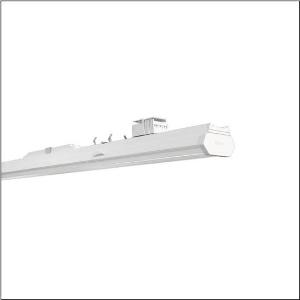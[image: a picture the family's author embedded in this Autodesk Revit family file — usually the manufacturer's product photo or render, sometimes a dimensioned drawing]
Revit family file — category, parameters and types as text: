
# Revit family: licross_r__21_protected_ho_52td13cn4c5s_0d58
name_source: partatom
category: Lighting Fixtures
units: mm (PartAtom-declared; Revit-internal decimal feet)

## family parameters
Cut with Voids When Loaded = No
Host = Face
Light Source = No
Part Type = Normal
Room Calculation Point = No
Round Connector Dimension = Use Diameter
Shared = No

## types (1)
- --- (1 x LED, 12680 lm, 68.9 W, 4000K)
    Apparent Load = 69 VA
    CIE Flux Codes = 89 96 99 100 99
    Color Rendering = 80
    Color Temperature = 4000K
    Default Elevation = 1800 mm
    Description = Licross® 21 Protected HO, luminaire insert, of sheet steel, galvanised, coil coated, white, length: 1.500mm, width: 66mm, height: 67mm, LED rated luminous flux: 12.690lm, light colour: 840, control gear: ON/OFF Multilumen, CLOi, control gear: ECG Multilumen, with plug, 3-pole, with phase selection, mains connection: 220..240V, AC, 50/60Hz, start of lifetime: 69W, end of service life: 83W, halogen-free wiring, primary light control with lens, of plastic, primary optical cover: cover, of PMMA, light emission: direct distribution, primary light characteristic: symmetric, protection rating (complete): IP54, insulation class (complete): insulation class I (protective earthing), certification: CE, ENEC, VDE, UKCA, protection symbol: D if used in an environment with non-conductive dust loads with corresponding accessories, impact resistance: IK06, permissible ambient temperature for indoor applications: -35..+35°C, corresponds to IFS (International Featured Standards) requirements for safety and quality in the food industry, reducing of maximum allowable ambient temperature of 5°C with ceiling mounting, LABS conformity tested according to VDMA 24364:2018-05, packaging unit: 1 piece
    Height = 92 mm
    Lamp = 1 x LED
    Lamp Light Flux = 12680 lm
    Lamp Power = 68.9 W
    Lamp count = 1
    Length = 1500 mm
    Luminous efficacy = 184 lm/W
    Manufacturer = Siteco
    ModVariant = No
    Model = 52TD13CN4C5S
    Mounting Place = Ceiling
    Mounting Type = Pendant
    Number of Poles = 1
    OnlyDefault = Yes
    Power Factor = 1
    Product Name = Licross® 21 Protected HO
    Product group = luminaire insert
    ProductGroupID = 901
    Protection Class = Protection class I
    Protection Degree = IP 54
    RLX_Detail_Level = 1
    RLX_Emergency_Light_Flux = 0 lm
    RLX_Emergency_Type = 0
    RLX_Emergency_Type_DB = No
    RlxData = <blob elided: 22021 chars, md5=b2d1db0e>
    Socket = socket
    Standby Power = 0 W
    System Light Flux = 12680 lm
    System Power = 69 W
    Type Comments = factory setting: luminous flux: 100 % | (A | C | E) | 162 mA
    Type Image = l_1256148.jpg
    URL = http://relux.com
    VarID = @adj_040929
    Voltage = 0 V
    Weight = 0.00 kg
    Width = 88 mm

## geometry (parser evidence)
native form markers: Blend x4, Sweep x10
no freeform markers — native parametric forms only
